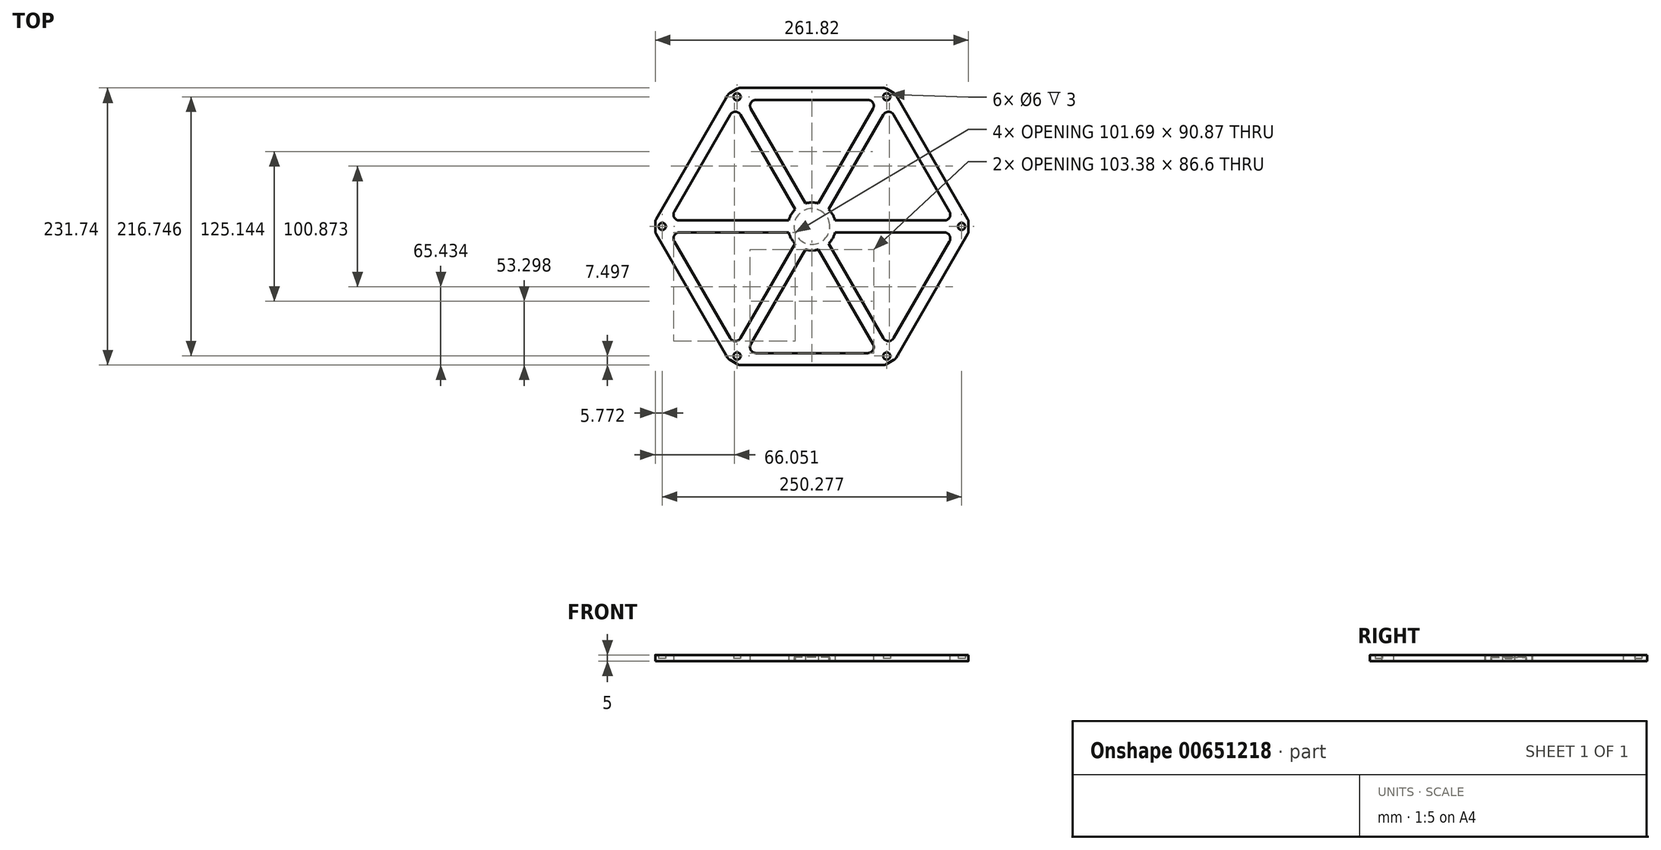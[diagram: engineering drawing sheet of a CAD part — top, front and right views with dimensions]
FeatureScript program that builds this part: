
annotation { "Feature Type Name" : "Feature", "Feature Type Description" : "" }
export const myFeature = defineFeature(function(context is Context, id is Id, definition is map)
    precondition{}
    {
        {
            var Q0;
            Q0=qCreatedBy(makeId("Top.planeOp"),FACE);
            var sketch = newSketch(context, id + "F0", { "sketchPlane" : qUnion([Q0])});
            skLineSegment(sketch, "E0", {"start": v(0, 0) * mm, "end": v(-20, 0) * mm, "construction": true});
            skLineSegment(sketch, "E1", {"start": v(0, 0) * mm, "end": v(20, 0) * mm, "construction": true});
            skLineSegment(sketch, "E2", {"start": v(0, 0) * mm, "end": v(-10, -17.32) * mm, "construction": true});
            skLineSegment(sketch, "E3", {"start": v(0, 0) * mm, "end": v(10, 17.32) * mm, "construction": true});
            skLineSegment(sketch, "E4", {"start": v(0, 0) * mm, "end": v(-10, 17.32) * mm, "construction": true});
            skLineSegment(sketch, "E5", {"start": v(-10, 17.32) * mm, "end": v(-60, 103.92) * mm, "construction": true});
            skLineSegment(sketch, "E6", {"start": v(-10, -17.32) * mm, "end": v(-59.68, -103.37) * mm, "construction": true});
            skLineSegment(sketch, "E7", {"start": v(-20, 0) * mm, "end": v(-119.36, 0) * mm, "construction": true});
            skLineSegment(sketch, "E8", {"start": v(10, -17.32) * mm, "end": v(60, -103.92) * mm, "construction": true});
            skLineSegment(sketch, "E9", {"start": v(20, 0) * mm, "end": v(120, 0) * mm, "construction": true});
            skLineSegment(sketch, "E10", {"start": v(10, 17.32) * mm, "end": v(60, 103.92) * mm, "construction": true});
            skLineSegment(sketch, "E11", {"start": v(0, 0) * mm, "end": v(10, -17.32) * mm, "construction": true});
            skPoint(sketch, "E12.center", {"position": v(0, 0) * mm});
            skLineSegment(sketch, "E13", {"start": v(-119.36, 0) * mm, "end": v(-119.36, 5) * mm});
            skLineSegment(sketch, "E14", {"start": v(-119.36, 0) * mm, "end": v(-119.36, -5) * mm});
            skLineSegment(sketch, "E15.1.0", {"start": v(-59.68, -103.37) * mm, "end": v(-64.01, -100.87) * mm});
            skLineSegment(sketch, "E15.1.1", {"start": v(-59.68, -103.37) * mm, "end": v(-55.35, -105.87) * mm});
            skLineSegment(sketch, "E15.2.0", {"start": v(59.68, -103.37) * mm, "end": v(55.35, -105.87) * mm});
            skLineSegment(sketch, "E15.2.1", {"start": v(59.68, -103.37) * mm, "end": v(64.01, -100.87) * mm});
            skLineSegment(sketch, "E15.3.0", {"start": v(119.36, 0) * mm, "end": v(119.36, -5) * mm});
            skLineSegment(sketch, "E15.3.1", {"start": v(119.36, 0) * mm, "end": v(119.36, 5) * mm});
            skLineSegment(sketch, "E15.4.0", {"start": v(59.68, 103.37) * mm, "end": v(64.01, 100.87) * mm});
            skLineSegment(sketch, "E15.4.1", {"start": v(59.68, 103.37) * mm, "end": v(55.35, 105.87) * mm});
            skLineSegment(sketch, "E15.5.0", {"start": v(-59.68, 103.37) * mm, "end": v(-55.35, 105.87) * mm});
            skLineSegment(sketch, "E15.5.1", {"start": v(-59.68, 103.37) * mm, "end": v(-64.01, 100.87) * mm});
            skLineSegment(sketch, "E16", {"start": v(-119.36, 5) * mm, "end": v(-19.36, 5) * mm});
            skLineSegment(sketch, "E17", {"start": v(-119.36, -5) * mm, "end": v(-19.36, -5) * mm});
            skLineSegment(sketch, "E18", {"start": v(-64.01, -100.87) * mm, "end": v(-14.01, -14.27) * mm});
            skLineSegment(sketch, "E19", {"start": v(55.35, -105.87) * mm, "end": v(5.35, -19.27) * mm});
            skLineSegment(sketch, "E20", {"start": v(64.01, -100.87) * mm, "end": v(14.01, -14.27) * mm});
            skLineSegment(sketch, "E21", {"start": v(119.36, -5) * mm, "end": v(19.36, -5) * mm});
            skLineSegment(sketch, "E22", {"start": v(119.36, 5) * mm, "end": v(19.36, 5) * mm});
            skLineSegment(sketch, "E23", {"start": v(64.01, 100.87) * mm, "end": v(14.01, 14.27) * mm});
            skLineSegment(sketch, "E24", {"start": v(55.35, 105.87) * mm, "end": v(5.35, 19.27) * mm});
            skLineSegment(sketch, "E25", {"start": v(-64.01, 100.87) * mm, "end": v(-14.01, 14.27) * mm});
            skLineSegment(sketch, "E26", {"start": v(-55.35, 105.87) * mm, "end": v(-5.35, 19.27) * mm});
            skLineSegment(sketch, "E27", {"start": v(-55.35, -105.87) * mm, "end": v(-5.35, -19.27) * mm});
            skLineSegment(sketch, "E28", {"start": v(-119.36, -5) * mm, "end": v(-64.01, -100.87) * mm});
            skLineSegment(sketch, "E29", {"start": v(-55.35, -105.87) * mm, "end": v(55.35, -105.87) * mm});
            skLineSegment(sketch, "E30", {"start": v(64.01, -100.87) * mm, "end": v(119.36, -5) * mm});
            skLineSegment(sketch, "E31", {"start": v(-119.36, 5) * mm, "end": v(-64.01, 100.87) * mm});
            skLineSegment(sketch, "E32", {"start": v(-55.35, 105.87) * mm, "end": v(55.35, 105.87) * mm});
            skLineSegment(sketch, "E33", {"start": v(64.01, 100.87) * mm, "end": v(119.36, 5) * mm});
            skLineSegment(sketch, "E34.0", {"start": v(-55.35, 115.87) * mm, "end": v(55.35, 115.87) * mm});
            skLineSegment(sketch, "E35.0", {"start": v(-128.03, 10) * mm, "end": v(-72.67, 105.87) * mm});
            skLineSegment(sketch, "E36.0", {"start": v(-128.03, -10) * mm, "end": v(-72.67, -105.87) * mm});
            skLineSegment(sketch, "E37.0", {"start": v(-55.35, -115.87) * mm, "end": v(55.35, -115.87) * mm});
            skLineSegment(sketch, "E38.0", {"start": v(72.67, 105.87) * mm, "end": v(128.03, 10) * mm});
            skLineSegment(sketch, "E39.0", {"start": v(72.67, -105.87) * mm, "end": v(128.03, -10) * mm});
            skLineSegment(sketch, "E40", {"start": v(-55.35, -105.87) * mm, "end": v(-60.58, -114.92) * mm, "construction": true});
            skLineSegment(sketch, "E41", {"start": v(-64.01, -100.87) * mm, "end": v(-71.06, -113.07) * mm, "construction": true});
            skLineSegment(sketch, "E42", {"start": v(-72.67, -105.87) * mm, "end": v(-69.79, -110.87) * mm});
            skLineSegment(sketch, "E43", {"start": v(-55.35, -115.87) * mm, "end": v(-61.13, -115.87) * mm});
            skLineSegment(sketch, "E44", {"start": v(-61.13, -115.87) * mm, "end": v(-69.79, -110.87) * mm});
            skLineSegment(sketch, "E45", {"start": v(55.35, -105.87) * mm, "end": v(63.7, -120.32) * mm, "construction": true});
            skLineSegment(sketch, "E46", {"start": v(64.01, -100.87) * mm, "end": v(72.67, -115.87) * mm, "construction": true});
            skLineSegment(sketch, "E47", {"start": v(119.36, -5) * mm, "end": v(134.72, -5) * mm, "construction": true});
            skLineSegment(sketch, "E48", {"start": v(119.36, 5) * mm, "end": v(137.91, 5) * mm, "construction": true});
            skLineSegment(sketch, "E49", {"start": v(55.35, 105.87) * mm, "end": v(62.63, 118.48) * mm, "construction": true});
            skLineSegment(sketch, "E50", {"start": v(64.01, 100.87) * mm, "end": v(72.34, 115.3) * mm, "construction": true});
            skLineSegment(sketch, "E51", {"start": v(-55.35, 105.87) * mm, "end": v(-62.75, 118.7) * mm, "construction": true});
            skLineSegment(sketch, "E52", {"start": v(-64.01, 100.87) * mm, "end": v(-72.33, 115.27) * mm, "construction": true});
            skLineSegment(sketch, "E53", {"start": v(-119.36, -5) * mm, "end": v(-137.37, -5) * mm, "construction": true});
            skLineSegment(sketch, "E54", {"start": v(-119.36, 5) * mm, "end": v(-137.37, 5) * mm, "construction": true});
            skLineSegment(sketch, "E55", {"start": v(-128.03, 10) * mm, "end": v(-130.91, 5) * mm});
            skLineSegment(sketch, "E56", {"start": v(-128.03, -10) * mm, "end": v(-130.91, -5) * mm});
            skLineSegment(sketch, "E57", {"start": v(-130.91, 5) * mm, "end": v(-130.91, -5) * mm});
            skLineSegment(sketch, "E58", {"start": v(55.35, -115.87) * mm, "end": v(61.13, -115.87) * mm});
            skLineSegment(sketch, "E59", {"start": v(72.67, -105.87) * mm, "end": v(69.79, -110.87) * mm});
            skLineSegment(sketch, "E60", {"start": v(61.13, -115.87) * mm, "end": v(69.79, -110.87) * mm});
            skLineSegment(sketch, "E61", {"start": v(128.03, -10) * mm, "end": v(130.91, -5) * mm});
            skLineSegment(sketch, "E62", {"start": v(128.03, 10) * mm, "end": v(130.91, 5) * mm});
            skLineSegment(sketch, "E63", {"start": v(130.91, 5) * mm, "end": v(130.91, -5) * mm});
            skLineSegment(sketch, "E64", {"start": v(55.35, 115.87) * mm, "end": v(61.13, 115.87) * mm});
            skLineSegment(sketch, "E65", {"start": v(61.13, 115.87) * mm, "end": v(69.79, 110.87) * mm});
            skLineSegment(sketch, "E66", {"start": v(69.79, 110.87) * mm, "end": v(72.67, 105.87) * mm});
            skLineSegment(sketch, "E67", {"start": v(-55.35, 115.87) * mm, "end": v(-61.13, 115.87) * mm});
            skLineSegment(sketch, "E68", {"start": v(-61.13, 115.87) * mm, "end": v(-69.79, 110.87) * mm});
            skLineSegment(sketch, "E69", {"start": v(-69.79, 110.87) * mm, "end": v(-72.67, 105.87) * mm});
            skLineSegment(sketch, "E70", {"start": v(-64.01, -100.87) * mm, "end": v(-61.13, -115.87) * mm, "construction": true});
            skLineSegment(sketch, "E71", {"start": v(-69.79, -110.87) * mm, "end": v(-55.35, -105.87) * mm, "construction": true});
            skPoint(sketch, "E72", {"position": v(-62.57, -108.37) * mm});
            skCircle(sketch, "E73", {"center": v(-62.57, -108.37) * mm, "radius": 3 * mm});
            skCircle(sketch, "E74.1.0", {"center": v(62.57, -108.37) * mm, "radius": 3 * mm});
            skCircle(sketch, "E74.2.0", {"center": v(125.14, 0) * mm, "radius": 3 * mm});
            skCircle(sketch, "E74.3.0", {"center": v(62.57, 108.37) * mm, "radius": 3 * mm});
            skCircle(sketch, "E74.4.0", {"center": v(-62.57, 108.37) * mm, "radius": 3 * mm});
            skCircle(sketch, "E74.5.0", {"center": v(-125.14, 0) * mm, "radius": 3 * mm});
            skPoint(sketch, "E75.start.orphan", {"position": v(-15.13, -5.38) * mm});
            skPoint(sketch, "E76.start.orphan", {"position": v(-12.22, -10.41) * mm});
            skPoint(sketch, "E77.orphan", {"position": v(18.59, 7.38) * mm});
            skCircle(sketch, "E78", {"center": v(0, 0) * mm, "radius": 20 * mm});
            skCircle(sketch, "E79", {"center": v(0, 0) * mm, "radius": 15 * mm});
            skSolve(sketch);
        }
        {
            var Q0;
            Q0=makeQuery(id+"F0.imprint","IMPRINT",FACE,{"disambiguationData":[TD([[makeQuery(id+"F0.imprint","IMPRINT",EDGE,{"derivedFrom":sQuery(id+"F0.wireOp",EDGE,"E13")}),1.0]])]});
            var Q1;
            {var subQ9=sQuery(id+"F0.wireOp",EDGE,"HfZjKeIH-J2he-E3ts-KsWi-W7cin7nE6oE4");Q1=makeQuery(id+"F0.imprint","IMPRINT",FACE,{"disambiguationData":[TD([[makeQuery(id+"F0.imprint","IMPRINT",EDGE,{"derivedFrom":subQ9}),1.0]])]});}
            var Q2;
            Q2=makeQuery(id+"F0.imprint","IMPRINT",FACE,{"disambiguationData":[TD([[makeQuery(id+"F0.imprint","IMPRINT",EDGE,{"derivedFrom":sQuery(id+"F0.wireOp",EDGE,"E15.5.0")}),-1.0]])]});
            var Q3;
            Q3=makeQuery(id+"F0.imprint","IMPRINT",FACE,{"disambiguationData":[TD([[makeQuery(id+"F0.imprint","IMPRINT",EDGE,{"derivedFrom":sQuery(id+"F0.wireOp",EDGE,"E15.4.0")}),-1.0]])]});
            var Q4;
            Q4=makeQuery(id+"F0.imprint","IMPRINT",FACE,{"disambiguationData":[TD([[makeQuery(id+"F0.imprint","IMPRINT",EDGE,{"derivedFrom":sQuery(id+"F0.wireOp",EDGE,"E15.3.0")}),-1.0]])]});
            var Q5;
            Q5=makeQuery(id+"F0.imprint","IMPRINT",FACE,{"disambiguationData":[TD([[makeQuery(id+"F0.imprint","IMPRINT",EDGE,{"derivedFrom":sQuery(id+"F0.wireOp",EDGE,"E15.2.0")}),-1.0]])]});
            var Q6;
            Q6=makeQuery(id+"F0.imprint","IMPRINT",FACE,{"disambiguationData":[TD([[makeQuery(id+"F0.imprint","IMPRINT",EDGE,{"derivedFrom":sQuery(id+"F0.wireOp",EDGE,"E15.1.0")}),-1.0]])]});
            var Q7;
            Q7=makeQuery(id+"F0.imprint","IMPRINT",FACE,{"disambiguationData":[TD([[makeQuery(id+"F0.imprint","IMPRINT",EDGE,{"derivedFrom":sQuery(id+"F0.wireOp",EDGE,"E13")}),-1.0]])]});
            extrude(context, id + "F1", {"entities" : qUnion([Q0, Q1, Q2, Q3, Q4, Q5, Q6, Q7]), "depth" : 5 * mm, "offsetDistance" : 25 * mm});
        }
        {
            var Q0;
            Q0=makeQuery(id+"F0.imprint","IMPRINT",FACE,{"disambiguationData":[TD([[makeQuery(id+"F0.imprint","IMPRINT",EDGE,{"derivedFrom":sQuery(id+"F0.wireOp",EDGE,"E74.5.0")}),1.0]])]});
            var Q1;
            Q1=makeQuery(id+"F0.imprint","IMPRINT",FACE,{"disambiguationData":[TD([[makeQuery(id+"F0.imprint","IMPRINT",EDGE,{"derivedFrom":sQuery(id+"F0.wireOp",EDGE,"E74.4.0")}),1.0]])]});
            var Q2;
            Q2=makeQuery(id+"F0.imprint","IMPRINT",FACE,{"disambiguationData":[TD([[makeQuery(id+"F0.imprint","IMPRINT",EDGE,{"derivedFrom":sQuery(id+"F0.wireOp",EDGE,"E74.3.0")}),1.0]])]});
            var Q3;
            Q3=makeQuery(id+"F0.imprint","IMPRINT",FACE,{"disambiguationData":[TD([[makeQuery(id+"F0.imprint","IMPRINT",EDGE,{"derivedFrom":sQuery(id+"F0.wireOp",EDGE,"E74.2.0")}),1.0]])]});
            var Q4;
            Q4=makeQuery(id+"F0.imprint","IMPRINT",FACE,{"disambiguationData":[TD([[makeQuery(id+"F0.imprint","IMPRINT",EDGE,{"derivedFrom":sQuery(id+"F0.wireOp",EDGE,"E74.1.0")}),1.0]])]});
            var Q5;
            Q5=makeQuery(id+"F0.imprint","IMPRINT",FACE,{"disambiguationData":[TD([[makeQuery(id+"F0.imprint","IMPRINT",EDGE,{"derivedFrom":sQuery(id+"F0.wireOp",EDGE,"E73")}),1.0]])]});
            extrude(context, id + "F2", {"entities" : qUnion([Q0, Q1, Q2, Q3, Q4, Q5]), "operationType" : NewBodyOperationType.ADD, "depth" : 2 * mm, "offsetDistance" : 25 * mm});
        }
        {
            var Q0;
            Q0=makeQuery(id+"F1.opExtrude","SWEPT_EDGE",EDGE,{"disambiguationData":[OSD([sQuery(id+"F0.wireOp",EDGE,"E55"),sQuery(id+"F0.wireOp",EDGE,"E57")])]});
            var Q1;
            Q1=makeQuery(id+"F1.opExtrude","SWEPT_EDGE",EDGE,{"disambiguationData":[OSD([sQuery(id+"F0.wireOp",EDGE,"E56"),sQuery(id+"F0.wireOp",EDGE,"E57")])]});
            var Q2;
            Q2=makeQuery(id+"F1.opExtrude","SWEPT_EDGE",EDGE,{"disambiguationData":[OSD([sQuery(id+"F0.wireOp",EDGE,"E42"),sQuery(id+"F0.wireOp",EDGE,"E44")])]});
            var Q3;
            Q3=makeQuery(id+"F1.opExtrude","SWEPT_EDGE",EDGE,{"disambiguationData":[OSD([sQuery(id+"F0.wireOp",EDGE,"E43"),sQuery(id+"F0.wireOp",EDGE,"E44")])]});
            var Q4;
            Q4=makeQuery(id+"F1.opExtrude","SWEPT_EDGE",EDGE,{"disambiguationData":[OSD([sQuery(id+"F0.wireOp",EDGE,"E58"),sQuery(id+"F0.wireOp",EDGE,"E60")])]});
            var Q5;
            Q5=makeQuery(id+"F1.opExtrude","SWEPT_EDGE",EDGE,{"disambiguationData":[OSD([sQuery(id+"F0.wireOp",EDGE,"E59"),sQuery(id+"F0.wireOp",EDGE,"E60")])]});
            var Q6;
            Q6=makeQuery(id+"F1.opExtrude","SWEPT_EDGE",EDGE,{"disambiguationData":[OSD([sQuery(id+"F0.wireOp",EDGE,"E61"),sQuery(id+"F0.wireOp",EDGE,"E63")])]});
            var Q7;
            Q7=makeQuery(id+"F1.opExtrude","SWEPT_EDGE",EDGE,{"disambiguationData":[OSD([sQuery(id+"F0.wireOp",EDGE,"E62"),sQuery(id+"F0.wireOp",EDGE,"E63")])]});
            var Q8;
            Q8=makeQuery(id+"F1.opExtrude","SWEPT_EDGE",EDGE,{"disambiguationData":[OSD([sQuery(id+"F0.wireOp",EDGE,"E65"),sQuery(id+"F0.wireOp",EDGE,"E66")])]});
            var Q9;
            Q9=makeQuery(id+"F1.opExtrude","SWEPT_EDGE",EDGE,{"disambiguationData":[OSD([sQuery(id+"F0.wireOp",EDGE,"E64"),sQuery(id+"F0.wireOp",EDGE,"E65")])]});
            var Q10;
            Q10=makeQuery(id+"F1.opExtrude","SWEPT_EDGE",EDGE,{"disambiguationData":[OSD([sQuery(id+"F0.wireOp",EDGE,"E67"),sQuery(id+"F0.wireOp",EDGE,"E68")])]});
            var Q11;
            Q11=makeQuery(id+"F1.opExtrude","SWEPT_EDGE",EDGE,{"disambiguationData":[OSD([sQuery(id+"F0.wireOp",EDGE,"E68"),sQuery(id+"F0.wireOp",EDGE,"E69")])]});
            fillet(context, id + "F3", {"entities" : qUnion([Q0, Q1, Q2, Q3, Q4, Q5, Q6, Q7, Q8, Q9, Q10, Q11]), "radius" : 5 * mm, "tangentPropagation" : true, "allowEdgeOverflow" : false});
        }
        {
            var Q0;
            Q0=makeQuery(id+"F1.opExtrude","SWEPT_EDGE",EDGE,{"disambiguationData":[OSD([sQuery(id+"F0.wireOp",EDGE,"E15.5.1"),sQuery(id+"F0.wireOp",EDGE,"E25"),sQuery(id+"F0.wireOp",EDGE,"E31")])]});
            var Q1;
            Q1=makeQuery(id+"F1.opExtrude","SWEPT_EDGE",EDGE,{"disambiguationData":[OSD([sQuery(id+"F0.wireOp",EDGE,"E15.5.0"),sQuery(id+"F0.wireOp",EDGE,"E26"),sQuery(id+"F0.wireOp",EDGE,"E32")])]});
            var Q2;
            Q2=makeQuery(id+"F1.opExtrude","SWEPT_EDGE",EDGE,{"disambiguationData":[OSD([sQuery(id+"F0.wireOp",EDGE,"E15.4.1"),sQuery(id+"F0.wireOp",EDGE,"E24"),sQuery(id+"F0.wireOp",EDGE,"E32")])]});
            var Q3;
            Q3=makeQuery(id+"F1.opExtrude","SWEPT_EDGE",EDGE,{"disambiguationData":[OSD([sQuery(id+"F0.wireOp",EDGE,"E15.4.0"),sQuery(id+"F0.wireOp",EDGE,"E23"),sQuery(id+"F0.wireOp",EDGE,"E33")])]});
            var Q4;
            Q4=makeQuery(id+"F1.opExtrude","SWEPT_EDGE",EDGE,{"disambiguationData":[OSD([sQuery(id+"F0.wireOp",EDGE,"E15.3.1"),sQuery(id+"F0.wireOp",EDGE,"E22"),sQuery(id+"F0.wireOp",EDGE,"E33")])]});
            var Q5;
            Q5=makeQuery(id+"F1.opExtrude","SWEPT_EDGE",EDGE,{"disambiguationData":[OSD([sQuery(id+"F0.wireOp",EDGE,"E15.3.0"),sQuery(id+"F0.wireOp",EDGE,"E21"),sQuery(id+"F0.wireOp",EDGE,"E30")])]});
            var Q6;
            Q6=makeQuery(id+"F1.opExtrude","SWEPT_EDGE",EDGE,{"disambiguationData":[OSD([sQuery(id+"F0.wireOp",EDGE,"E15.2.1"),sQuery(id+"F0.wireOp",EDGE,"E20"),sQuery(id+"F0.wireOp",EDGE,"E30")])]});
            var Q7;
            Q7=makeQuery(id+"F1.opExtrude","SWEPT_EDGE",EDGE,{"disambiguationData":[OSD([sQuery(id+"F0.wireOp",EDGE,"E15.2.0"),sQuery(id+"F0.wireOp",EDGE,"E19"),sQuery(id+"F0.wireOp",EDGE,"E29")])]});
            var Q8;
            Q8=makeQuery(id+"F1.opExtrude","SWEPT_EDGE",EDGE,{"disambiguationData":[OSD([sQuery(id+"F0.wireOp",EDGE,"E15.1.1"),sQuery(id+"F0.wireOp",EDGE,"E27"),sQuery(id+"F0.wireOp",EDGE,"E29")])]});
            var Q9;
            Q9=makeQuery(id+"F1.opExtrude","SWEPT_EDGE",EDGE,{"disambiguationData":[OSD([sQuery(id+"F0.wireOp",EDGE,"E15.1.0"),sQuery(id+"F0.wireOp",EDGE,"E18"),sQuery(id+"F0.wireOp",EDGE,"E28")])]});
            var Q10;
            Q10=makeQuery(id+"F1.opExtrude","SWEPT_EDGE",EDGE,{"disambiguationData":[OSD([sQuery(id+"F0.wireOp",EDGE,"E14"),sQuery(id+"F0.wireOp",EDGE,"E17"),sQuery(id+"F0.wireOp",EDGE,"E28")])]});
            var Q11;
            Q11=makeQuery(id+"F1.opExtrude","SWEPT_EDGE",EDGE,{"disambiguationData":[OSD([sQuery(id+"F0.wireOp",EDGE,"E13"),sQuery(id+"F0.wireOp",EDGE,"E16"),sQuery(id+"F0.wireOp",EDGE,"E31")])]});
            fillet(context, id + "F4", {"entities" : qUnion([Q0, Q1, Q2, Q3, Q4, Q5, Q6, Q7, Q8, Q9, Q10, Q11]), "radius" : 5 * mm, "tangentPropagation" : true, "allowEdgeOverflow" : false});
        }
        {
            var Q0;
            {var subQ0=sQuery(id+"F0.wireOp",EDGE,"E78");var subQ8=makeQuery(id+"F0.imprint","INTERSECT",VERTEX,{"derivedFrom":[sQuery(id+"F0.wireOp",EDGE,"E22"),subQ0]});Q0=makeQuery(id+"F0.imprint","IMPRINT",FACE,{"disambiguationData":[TD([[makeQuery(id+"F0.imprint","IMPRINT",EDGE,{"disambiguationData":[TD([[subQ8,-1.0]])],"derivedFrom":subQ0}),1.0]])]});}
            extrude(context, id + "F5", {"entities" : qUnion([Q0]), "operationType" : NewBodyOperationType.ADD, "depth" : 5 * mm, "offsetDistance" : 25 * mm});
        }
        {
            var Q0;
            Q0=makeQuery(id+"F0.imprint","IMPRINT",FACE,{"disambiguationData":[TD([[makeQuery(id+"F0.imprint","IMPRINT",EDGE,{"derivedFrom":sQuery(id+"F0.wireOp",EDGE,"E79")}),1.0]])]});
            extrude(context, id + "F6", {"entities" : qUnion([Q0]), "operationType" : NewBodyOperationType.ADD, "depth" : 5 * mm, "offsetDistance" : 25 * mm});
        }
        {
            var Q0;
            Q0=makeQuery(id+"F0.imprint","IMPRINT",FACE,{"disambiguationData":[TD([[makeQuery(id+"F0.imprint","IMPRINT",EDGE,{"derivedFrom":sQuery(id+"F0.wireOp",EDGE,"E79")}),1.0]])]});
            extrude(context, id + "F7", {"entities" : qUnion([Q0]), "operationType" : NewBodyOperationType.REMOVE, "depth" : 3 * mm, "offsetDistance" : 25 * mm});
        }
    });
